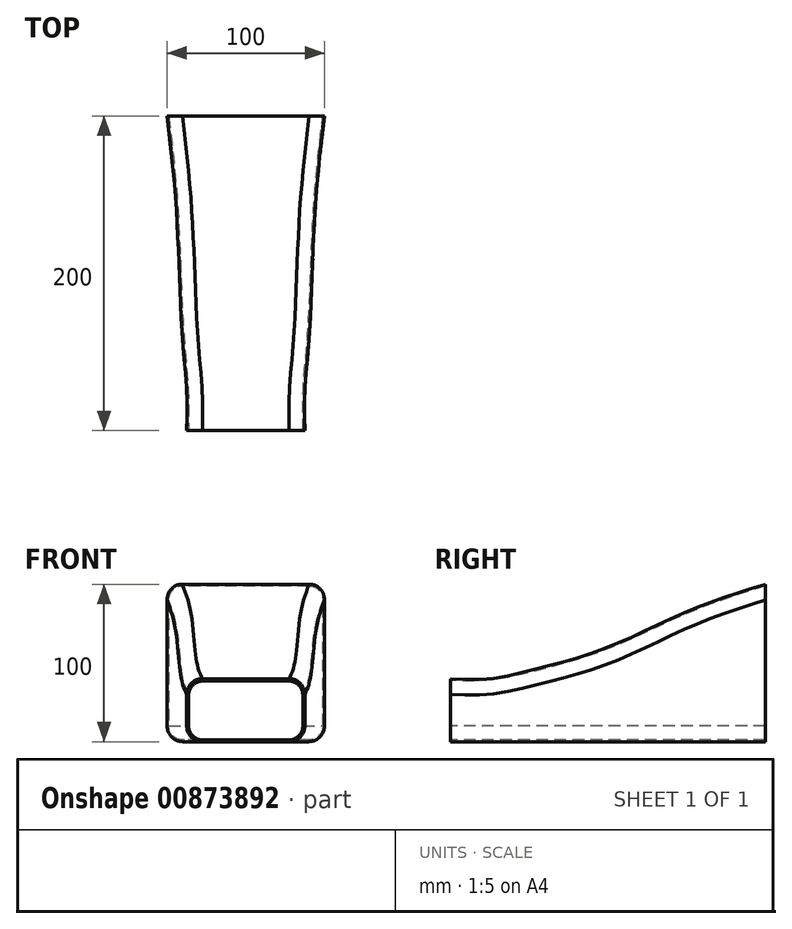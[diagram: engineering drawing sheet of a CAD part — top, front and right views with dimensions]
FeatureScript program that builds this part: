
annotation { "Feature Type Name" : "Feature", "Feature Type Description" : "" }
export const myFeature = defineFeature(function(context is Context, id is Id, definition is map)
    precondition{}
    {
        {
            var Q0;
            Q0=qCreatedBy(makeId("Front.planeOp"),FACE);
            var sketch = newSketch(context, id + "F0", { "sketchPlane" : qUnion([Q0])});
            skLineSegment(sketch, "E0.bottom", {"start": v(50, -50) * mm, "end": v(-50, -50) * mm});
            skLineSegment(sketch, "E0.top", {"start": v(50, 50) * mm, "end": v(-50, 50) * mm});
            skLineSegment(sketch, "E0.left", {"start": v(50, -50) * mm, "end": v(50, 50) * mm});
            skLineSegment(sketch, "E0.right", {"start": v(-50, -50) * mm, "end": v(-50, 50) * mm});
            skPoint(sketch, "E0.middle", {"position": v(0, 0) * mm});
            skSolve(sketch);
        }
        {
            var Q0;
            Q0=qCreatedBy(makeId("Front.planeOp"),FACE);
            cPlane(context, id + "F1", {"entities" : qUnion([Q0]), "cplaneType" : CPlaneType.OFFSET, "offset" : 200 * mm, "width" : 150 * mm, "height" : 150 * mm});
        }
        {
            var Q0;
            Q0=qCreatedBy(id+"F1.planeOp",FACE);
            var sketch = newSketch(context, id + "F2", { "sketchPlane" : qUnion([Q0])});
            skLineSegment(sketch, "E1.0.0", {"start": v(50, -50) * mm, "end": v(50, 50) * mm, "construction": true});
            skLineSegment(sketch, "E1.0.1", {"start": v(50, 50) * mm, "end": v(-50, 50) * mm, "construction": true});
            skLineSegment(sketch, "E1.0.2", {"start": v(-50, 50) * mm, "end": v(-50, -50) * mm, "construction": true});
            skLineSegment(sketch, "E1.0.3", {"start": v(-50, -50) * mm, "end": v(50, -50) * mm, "construction": true});
            skLineSegment(sketch, "E2.bottom", {"start": v(-37.5, -50) * mm, "end": v(37.5, -50) * mm});
            skLineSegment(sketch, "E2.top", {"start": v(-37.5, -10) * mm, "end": v(37.5, -10) * mm});
            skLineSegment(sketch, "E2.left", {"start": v(-37.5, -50) * mm, "end": v(-37.5, -10) * mm});
            skLineSegment(sketch, "E2.right", {"start": v(37.5, -50) * mm, "end": v(37.5, -10) * mm});
            skPoint(sketch, "E3", {"position": v(0, -10) * mm});
            skSolve(sketch);
        }
        {
            var Q0;
            Q0=qCreatedBy(id+"F1.planeOp",FACE);
            cPlane(context, id + "F3", {"entities" : qUnion([Q0]), "cplaneType" : CPlaneType.OFFSET, "offset" : 25 * mm, "oppositeDirection" : true, "width" : 150 * mm, "height" : 150 * mm});
        }
        {
            var Q0;
            Q0=qCreatedBy(id+"F3.planeOp",FACE);
            var sketch = newSketch(context, id + "F4", { "sketchPlane" : qUnion([Q0])});
            skLineSegment(sketch, "E4.0.0", {"start": v(37.5, -10) * mm, "end": v(-37.5, -10) * mm});
            skLineSegment(sketch, "E4.0.1", {"start": v(-37.5, -10) * mm, "end": v(-37.5, -50) * mm});
            skLineSegment(sketch, "E4.0.2", {"start": v(-37.5, -50) * mm, "end": v(37.5, -50) * mm});
            skLineSegment(sketch, "E4.0.3", {"start": v(37.5, -50) * mm, "end": v(37.5, -10) * mm});
            skSolve(sketch);
        }
        {
            var Q0;
            Q0=qCreatedBy(id+"F3.planeOp",FACE);
            cPlane(context, id + "F5", {"entities" : qUnion([Q0]), "cplaneType" : CPlaneType.OFFSET, "offset" : 25 * mm, "oppositeDirection" : true, "width" : 150 * mm, "height" : 150 * mm});
        }
        {
            var Q0;
            Q0=qCreatedBy(id+"F5.planeOp",FACE);
            var sketch = newSketch(context, id + "F6", { "sketchPlane" : qUnion([Q0])});
            skLineSegment(sketch, "E5.0.0", {"start": v(-37.5, -50) * mm, "end": v(37.5, -50) * mm, "construction": true});
            skLineSegment(sketch, "E5.0.1", {"start": v(37.5, -50) * mm, "end": v(37.5, -10) * mm, "construction": true});
            skLineSegment(sketch, "E5.0.2", {"start": v(37.5, -10) * mm, "end": v(-37.5, -10) * mm, "construction": true});
            skLineSegment(sketch, "E5.0.3", {"start": v(-37.5, -10) * mm, "end": v(-37.5, -50) * mm, "construction": true});
            skLineSegment(sketch, "E6", {"start": v(-39.5, -50) * mm, "end": v(-39.5, -5) * mm});
            skLineSegment(sketch, "E7", {"start": v(-39.5, -5) * mm, "end": v(39.5, -5) * mm});
            skLineSegment(sketch, "E8", {"start": v(39.5, -5) * mm, "end": v(39.5, -50) * mm});
            skLineSegment(sketch, "E9", {"start": v(39.5, -50) * mm, "end": v(-39.5, -50) * mm});
            skPoint(sketch, "E10", {"position": v(0, -5) * mm});
            skSolve(sketch);
        }
        {
            var Q0;
            Q0=qCreatedBy(id+"F5.planeOp",FACE);
            cPlane(context, id + "F7", {"entities" : qUnion([Q0]), "cplaneType" : CPlaneType.OFFSET, "offset" : 50 * mm, "oppositeDirection" : true, "width" : 150 * mm, "height" : 150 * mm});
        }
        {
            var Q0;
            Q0=qCreatedBy(id+"F7.planeOp",FACE);
            var sketch = newSketch(context, id + "F8", { "sketchPlane" : qUnion([Q0])});
            skLineSegment(sketch, "E11.0.0", {"start": v(-39.5, -50) * mm, "end": v(39.5, -50) * mm, "construction": true});
            skLineSegment(sketch, "E11.0.1", {"start": v(39.5, -50) * mm, "end": v(39.5, -5) * mm, "construction": true});
            skLineSegment(sketch, "E11.0.2", {"start": v(39.5, -5) * mm, "end": v(-39.5, -5) * mm, "construction": true});
            skLineSegment(sketch, "E11.0.3", {"start": v(-39.5, -5) * mm, "end": v(-39.5, -50) * mm, "construction": true});
            skLineSegment(sketch, "E12.0", {"start": v(-37.5, -10) * mm, "end": v(-37.5, -50) * mm, "construction": true});
            skLineSegment(sketch, "E13.0", {"start": v(37.5, -10) * mm, "end": v(-37.5, -10) * mm, "construction": true});
            skLineSegment(sketch, "E14.0", {"start": v(37.5, -50) * mm, "end": v(37.5, -10) * mm, "construction": true});
            skLineSegment(sketch, "E15", {"start": v(-42.25, -50) * mm, "end": v(-42.25, 10) * mm});
            skLineSegment(sketch, "E16", {"start": v(-42.25, 10) * mm, "end": v(42.25, 10) * mm});
            skLineSegment(sketch, "E17", {"start": v(42.25, 10) * mm, "end": v(42.25, -50) * mm});
            skLineSegment(sketch, "E18", {"start": v(42.25, -50) * mm, "end": v(-42.25, -50) * mm});
            skPoint(sketch, "E19", {"position": v(0, 10) * mm});
            skSolve(sketch);
        }
        {
            var Q0;
            Q0=qCreatedBy(id+"F7.planeOp",FACE);
            cPlane(context, id + "F9", {"entities" : qUnion([Q0]), "cplaneType" : CPlaneType.OFFSET, "offset" : 50 * mm, "oppositeDirection" : true, "width" : 150 * mm, "height" : 150 * mm});
        }
        {
            var Q0;
            Q0=qCreatedBy(id+"F9.planeOp",FACE);
            var sketch = newSketch(context, id + "F10", { "sketchPlane" : qUnion([Q0])});
            skLineSegment(sketch, "E20.0", {"start": v(42.25, -50) * mm, "end": v(-42.25, -50) * mm, "construction": true});
            skLineSegment(sketch, "E21.0", {"start": v(-42.25, -50) * mm, "end": v(-42.25, 10) * mm, "construction": true});
            skLineSegment(sketch, "E22.0", {"start": v(-42.25, 10) * mm, "end": v(42.25, 10) * mm, "construction": true});
            skLineSegment(sketch, "E23.0", {"start": v(42.25, 10) * mm, "end": v(42.25, -50) * mm, "construction": true});
            skLineSegment(sketch, "E24", {"start": v(-44.75, -50) * mm, "end": v(-44.75, 32.5) * mm});
            skLineSegment(sketch, "E25", {"start": v(-44.75, 32.5) * mm, "end": v(44.75, 32.5) * mm});
            skLineSegment(sketch, "E26", {"start": v(44.75, 32.5) * mm, "end": v(44.75, -50) * mm});
            skLineSegment(sketch, "E27", {"start": v(44.75, -50) * mm, "end": v(-44.75, -50) * mm});
            skPoint(sketch, "E28", {"position": v(0, 32.5) * mm});
            skPoint(sketch, "E29", {"position": v(0, 10) * mm});
            skSolve(sketch);
        }
        {
            var Q0;
            Q0=makeQuery(id+"F0.imprint","IMPRINT",FACE,{"disambiguationData":[TD([[makeQuery(id+"F0.imprint","IMPRINT",EDGE,{"derivedFrom":sQuery(id+"F0.wireOp",EDGE,"E0.bottom")}),-1.0]])]});
            var Q1;
            Q1=makeQuery(id+"F10.imprint","IMPRINT",FACE,{"disambiguationData":[TD([[makeQuery(id+"F10.imprint","IMPRINT",EDGE,{"derivedFrom":sQuery(id+"F10.wireOp",EDGE,"E24")}),-1.0]])]});
            var Q2;
            Q2=makeQuery(id+"F8.imprint","IMPRINT",FACE,{"disambiguationData":[TD([[makeQuery(id+"F8.imprint","IMPRINT",EDGE,{"derivedFrom":sQuery(id+"F8.wireOp",EDGE,"E15")}),-1.0]])]});
            var Q3;
            Q3=makeQuery(id+"F6.imprint","IMPRINT",FACE,{"disambiguationData":[TD([[makeQuery(id+"F6.imprint","IMPRINT",EDGE,{"derivedFrom":sQuery(id+"F6.wireOp",EDGE,"E6")}),-1.0]])]});
            var Q4;
            Q4=makeQuery(id+"F4.imprint","IMPRINT",FACE,{"disambiguationData":[TD([[makeQuery(id+"F4.imprint","IMPRINT",EDGE,{"derivedFrom":sQuery(id+"F4.wireOp",EDGE,"E4.0.0")}),1.0]])]});
            var Q5;
            Q5=makeQuery(id+"F2.imprint","IMPRINT",FACE,{"disambiguationData":[TD([[makeQuery(id+"F2.imprint","IMPRINT",EDGE,{"derivedFrom":sQuery(id+"F2.wireOp",EDGE,"E2.bottom")}),1.0]])]});
            loft(context, id + "F11", {"sheetProfilesArray" : [{ "sheetProfileEntities" : qUnion([Q0]) }, { "sheetProfileEntities" : qUnion([Q1]) }, { "sheetProfileEntities" : qUnion([Q2]) }, { "sheetProfileEntities" : qUnion([Q3]) }, { "sheetProfileEntities" : qUnion([Q4]) }, { "sheetProfileEntities" : qUnion([Q5]) }]});
        }
        {
            var Q0;
            Q0=makeQuery(id+"F11.opLoft","SWEPT_EDGE",EDGE,{"disambiguationData":[OSD([sQuery(id+"F0.wireOp",EDGE,"E0.top"),sQuery(id+"F0.wireOp",EDGE,"E0.left"),sQuery(id+"F2.wireOp",EDGE,"E2.top"),sQuery(id+"F2.wireOp",EDGE,"E2.right"),sQuery(id+"F4.wireOp",EDGE,"E4.0.0"),sQuery(id+"F4.wireOp",EDGE,"E4.0.3"),sQuery(id+"F6.wireOp",EDGE,"E7"),sQuery(id+"F6.wireOp",EDGE,"E8"),sQuery(id+"F8.wireOp",EDGE,"E16"),sQuery(id+"F8.wireOp",EDGE,"E17"),sQuery(id+"F10.wireOp",EDGE,"E25"),sQuery(id+"F10.wireOp",EDGE,"E26")])]});
            var Q1;
            Q1=makeQuery(id+"F11.opLoft","SWEPT_EDGE",EDGE,{"disambiguationData":[OSD([sQuery(id+"F0.wireOp",EDGE,"E0.top"),sQuery(id+"F0.wireOp",EDGE,"E0.right"),sQuery(id+"F2.wireOp",EDGE,"E2.top"),sQuery(id+"F2.wireOp",EDGE,"E2.left"),sQuery(id+"F4.wireOp",EDGE,"E4.0.0"),sQuery(id+"F4.wireOp",EDGE,"E4.0.1"),sQuery(id+"F6.wireOp",EDGE,"E6"),sQuery(id+"F6.wireOp",EDGE,"E7"),sQuery(id+"F8.wireOp",EDGE,"E15"),sQuery(id+"F8.wireOp",EDGE,"E16"),sQuery(id+"F10.wireOp",EDGE,"E24"),sQuery(id+"F10.wireOp",EDGE,"E25")])]});
            var Q2;
            Q2=makeQuery(id+"F11.opLoft","SWEPT_EDGE",EDGE,{"disambiguationData":[OSD([sQuery(id+"F0.wireOp",EDGE,"E0.bottom"),sQuery(id+"F0.wireOp",EDGE,"E0.left"),sQuery(id+"F2.wireOp",EDGE,"E2.bottom"),sQuery(id+"F2.wireOp",EDGE,"E2.right"),sQuery(id+"F4.wireOp",EDGE,"E4.0.2"),sQuery(id+"F4.wireOp",EDGE,"E4.0.3"),sQuery(id+"F6.wireOp",EDGE,"E8"),sQuery(id+"F6.wireOp",EDGE,"E9"),sQuery(id+"F8.wireOp",EDGE,"E17"),sQuery(id+"F8.wireOp",EDGE,"E18"),sQuery(id+"F10.wireOp",EDGE,"E26"),sQuery(id+"F10.wireOp",EDGE,"E27")])]});
            var Q3;
            Q3=makeQuery(id+"F11.opLoft","SWEPT_EDGE",EDGE,{"disambiguationData":[OSD([sQuery(id+"F0.wireOp",EDGE,"E0.bottom"),sQuery(id+"F0.wireOp",EDGE,"E0.right"),sQuery(id+"F2.wireOp",EDGE,"E2.bottom"),sQuery(id+"F2.wireOp",EDGE,"E2.left"),sQuery(id+"F4.wireOp",EDGE,"E4.0.1"),sQuery(id+"F4.wireOp",EDGE,"E4.0.2"),sQuery(id+"F6.wireOp",EDGE,"E6"),sQuery(id+"F6.wireOp",EDGE,"E9"),sQuery(id+"F8.wireOp",EDGE,"E15"),sQuery(id+"F8.wireOp",EDGE,"E18"),sQuery(id+"F10.wireOp",EDGE,"E24"),sQuery(id+"F10.wireOp",EDGE,"E27")])]});
            fillet(context, id + "F12", {"entities" : qUnion([Q0, Q1, Q2, Q3]), "radius" : 10 * mm, "tangentPropagation" : true, "allowEdgeOverflow" : false});
        }
        {
            var Q0;
            Q0=makeQuery(id+"F11.opLoft","CAP_FACE",FACE,{"disambiguationData":[OSD([makeQuery(id+"F2.imprint","IMPRINT",FACE,{"disambiguationData":[TD([[makeQuery(id+"F2.imprint","IMPRINT",EDGE,{"derivedFrom":sQuery(id+"F2.wireOp",EDGE,"E2.bottom")}),1.0]])]})])],"isStart":true});
            var Q1;
            Q1=makeQuery(id+"F11.opLoft","CAP_FACE",FACE,{"disambiguationData":[OSD([makeQuery(id+"F0.imprint","IMPRINT",FACE,{"disambiguationData":[TD([[makeQuery(id+"F0.imprint","IMPRINT",EDGE,{"derivedFrom":sQuery(id+"F0.wireOp",EDGE,"E0.bottom")}),-1.0]])]})])],"isStart":true});
            shell(context, id + "F13", {"entities" : qUnion([Q0, Q1]), "thickness" : 1 * mm});
        }
    });
